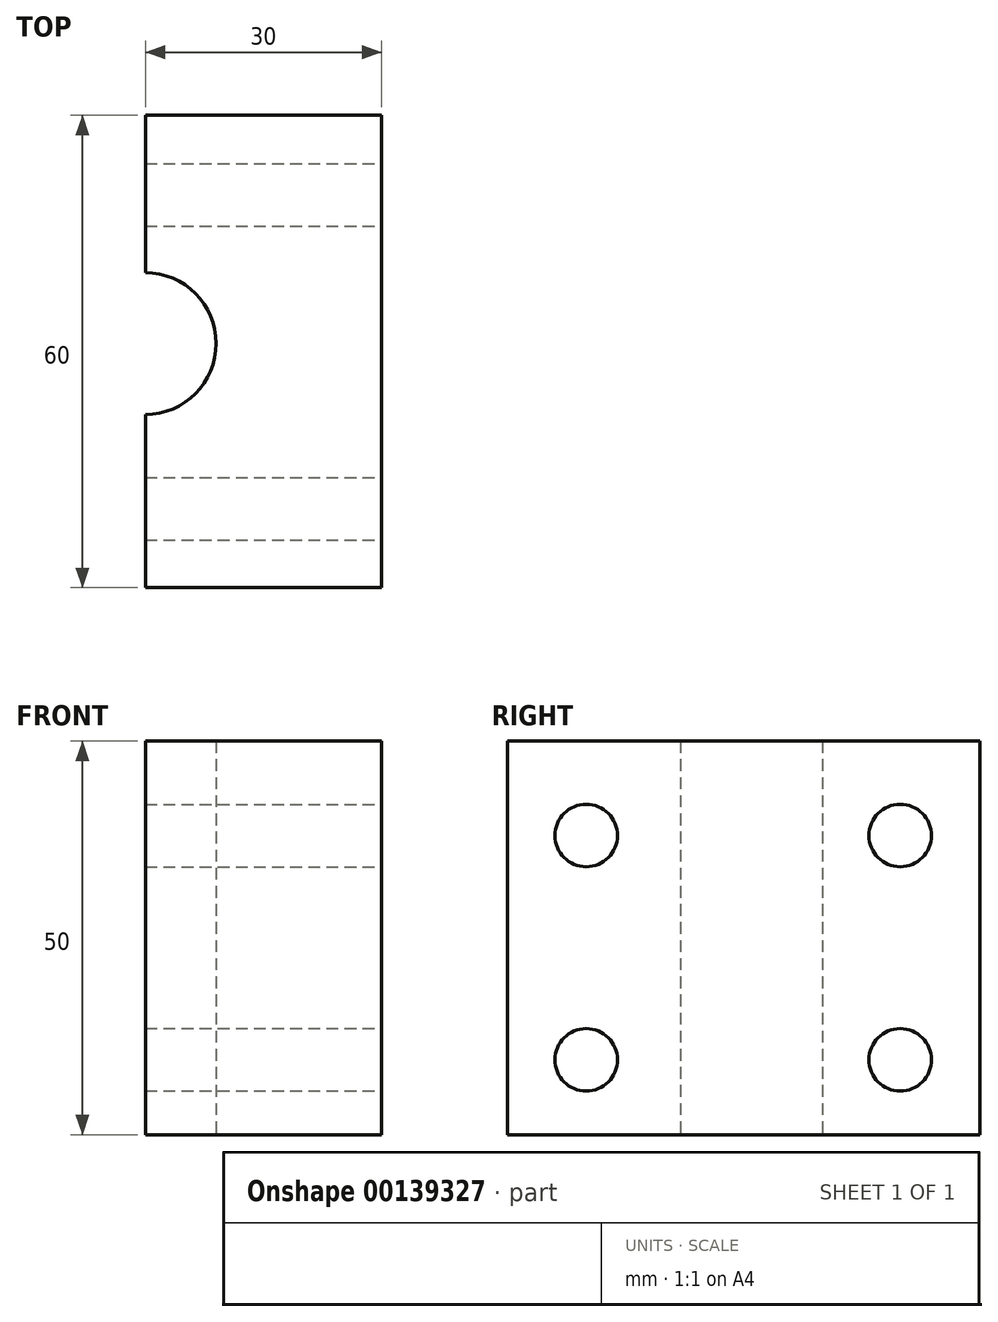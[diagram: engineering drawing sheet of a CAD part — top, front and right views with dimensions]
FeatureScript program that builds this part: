
annotation { "Feature Type Name" : "Feature", "Feature Type Description" : "" }
export const myFeature = defineFeature(function(context is Context, id is Id, definition is map)
    precondition{}
    {
        {
            var Q0;
            Q0=qCreatedBy(makeId("Top.planeOp"),FACE);
            var sketch = newSketch(context, id + "F0", { "sketchPlane" : qUnion([Q0])});
            skArc(sketch, "E0", {"start": v(0, -9) * mm, "mid": v(9, 0) * mm, "end": v(0, 9) * mm});
            skLineSegment(sketch, "E1", {"start": v(0, 9) * mm, "end": v(0, 29) * mm});
            skLineSegment(sketch, "E2", {"start": v(0, 29) * mm, "end": v(30, 29) * mm});
            skLineSegment(sketch, "E3", {"start": v(30, 29) * mm, "end": v(30, -31) * mm});
            skLineSegment(sketch, "E4", {"start": v(30, -31) * mm, "end": v(0, -31) * mm});
            skLineSegment(sketch, "E5", {"start": v(0, -31) * mm, "end": v(0, -9) * mm});
            skSolve(sketch);
        }
        {
            var Q0;
            Q0=makeQuery(id+"F0.imprint","IMPRINT",FACE,{"disambiguationData":[TD([[makeQuery(id+"F0.imprint","IMPRINT",EDGE,{"derivedFrom":sQuery(id+"F0.wireOp",EDGE,"E0")}),-1.0]])]});
            extrude(context, id + "F1", {"entities" : qUnion([Q0]), "depth" : 50 * mm});
        }
        {
            var Q0;
            Q0=makeQuery(id+"F1.opExtrude","SWEPT_FACE",FACE,{"disambiguationData":[OSD([sQuery(id+"F0.wireOp",EDGE,"E3")])]});
            var sketch = newSketch(context, id + "F2", { "sketchPlane" : qUnion([Q0])});
            skPoint(sketch, "E6", {"position": v(-21, 38) * mm});
            skPoint(sketch, "E7", {"position": v(-21, 9.5) * mm});
            skPoint(sketch, "E8", {"position": v(18.89, 38) * mm});
            skPoint(sketch, "E9", {"position": v(18.89, 9.5) * mm});
            skSolve(sketch);
        }
        {
            var Q0;
            Q0=sQuery(id+"F2.wireOp",VERTEX,"E6");
            var Q1;
            Q1=sQuery(id+"F2.wireOp",VERTEX,"E7");
            var Q2;
            Q2=sQuery(id+"F2.wireOp",VERTEX,"E8");
            var Q3;
            Q3=sQuery(id+"F2.wireOp",VERTEX,"E9");
            var Q4;
            Q4=makeQuery(id+"F1.opExtrude","SWEPT_BODY",BODY,{"disambiguationData":[OSD([sQuery(id+"F0.wireOp",EDGE,"E0"),sQuery(id+"F0.wireOp",EDGE,"E1"),sQuery(id+"F0.wireOp",EDGE,"E2"),sQuery(id+"F0.wireOp",EDGE,"E3"),sQuery(id+"F0.wireOp",EDGE,"E4"),sQuery(id+"F0.wireOp",EDGE,"E5")])]});
            hole(context, id + "F3", {"style" : HoleStyle.SIMPLE, "endStyle" : HoleEndStyle.THROUGH, "standardTappedOrClearance" : lookupTablePath({ "standard" : "ANSI", "engagement" : "75%", "pitch" : "16 tpi", "size" : "3/8", "type" : "Tapped" }), "standardBlindInLast" : lookupTablePath({ "standard" : "ANSI", "engagement" : "75%", "pitch" : "16 tpi", "size" : "3/8", "type" : "Tapped" }), "holeDiameter" : 7.94 * mm, "locations" : qUnion([Q0, Q1, Q2, Q3]), "scope" : qUnion([Q4]), "isTappedThrough" : true, "majorDiameter" : 9.53 * mm, "showTappedDepth" : true});
        }
    });
